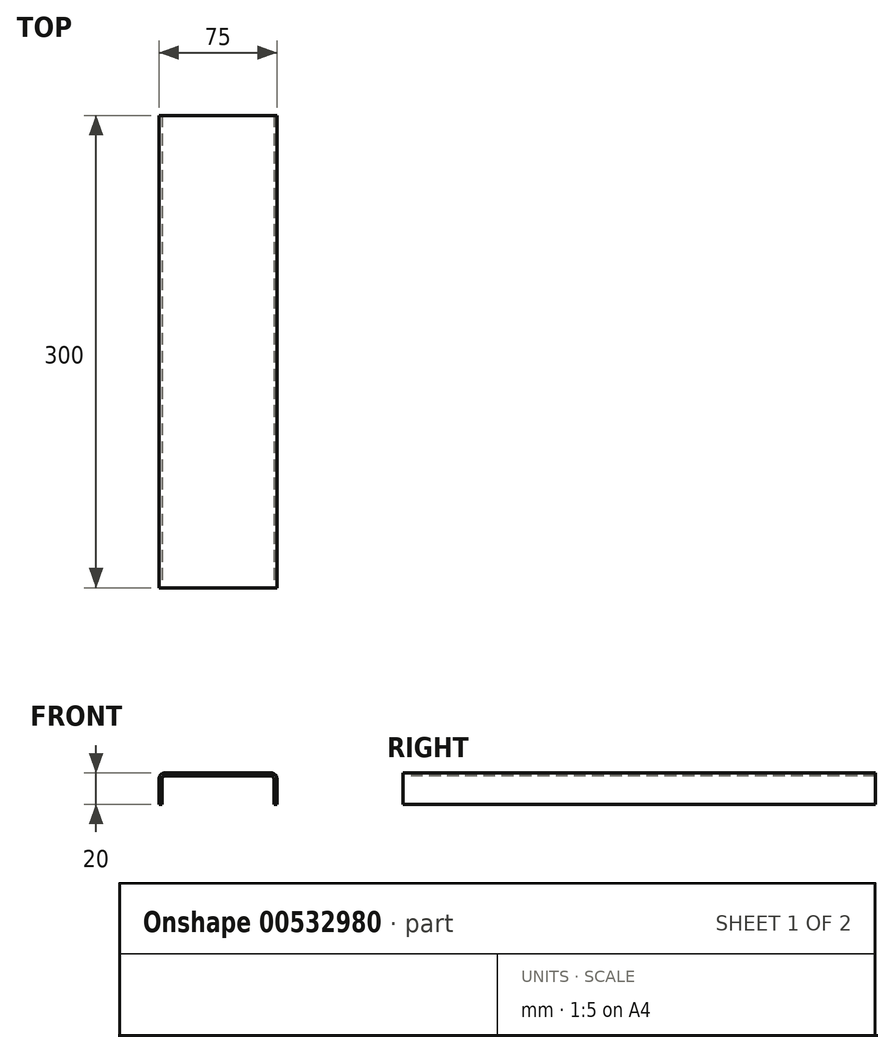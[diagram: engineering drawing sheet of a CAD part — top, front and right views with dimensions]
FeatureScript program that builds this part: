
annotation { "Feature Type Name" : "Feature", "Feature Type Description" : "" }
export const myFeature = defineFeature(function(context is Context, id is Id, definition is map)
    precondition{}
    {
        {
            var Q0;
            Q0=qCreatedBy(makeId("Front.planeOp"),FACE);
            var sketch = newSketch(context, id + "F0", { "sketchPlane" : qUnion([Q0])});
            skLineSegment(sketch, "E0", {"start": v(-85.73, 0) * mm, "end": v(-85.73, 16) * mm});
            skLineSegment(sketch, "E1", {"start": v(-81.73, 20) * mm, "end": v(-14.73, 20) * mm});
            skLineSegment(sketch, "E2", {"start": v(-10.73, 16) * mm, "end": v(-10.73, 0) * mm});
            skLineSegment(sketch, "E3.0", {"start": v(-12.73, 16) * mm, "end": v(-12.73, 0) * mm});
            skLineSegment(sketch, "E4.0", {"start": v(-81.73, 18) * mm, "end": v(-14.73, 18) * mm});
            skLineSegment(sketch, "E5.0", {"start": v(-83.73, 0) * mm, "end": v(-83.73, 16) * mm});
            skLineSegment(sketch, "E6", {"start": v(-83.73, 0) * mm, "end": v(-85.73, 0) * mm});
            skLineSegment(sketch, "E7", {"start": v(-10.73, 0) * mm, "end": v(-12.73, 0) * mm});
            skPoint(sketch, "E8.visualSharp", {"position": v(-12.73, 18) * mm});
            skArc(sketch, "E8.filletArc", {"start": v(-12.73, 16) * mm, "mid": v(-13.32, 17.41) * mm, "end": v(-14.73, 18) * mm});
            skPoint(sketch, "E9.visualSharp", {"position": v(-83.73, 18) * mm});
            skArc(sketch, "E9.filletArc", {"start": v(-81.73, 18) * mm, "mid": v(-83.15, 17.41) * mm, "end": v(-83.73, 16) * mm});
            skPoint(sketch, "E10.visualSharp", {"position": v(-85.73, 20) * mm});
            skArc(sketch, "E10.filletArc", {"start": v(-81.73, 20) * mm, "mid": v(-84.56, 18.83) * mm, "end": v(-85.73, 16) * mm});
            skPoint(sketch, "E11.visualSharp", {"position": v(-10.73, 20) * mm});
            skArc(sketch, "E11.filletArc", {"start": v(-10.73, 16) * mm, "mid": v(-11.9, 18.83) * mm, "end": v(-14.73, 20) * mm});
            skSolve(sketch);
        }
        {
            var Q0;
            Q0=makeQuery(id+"F0.imprint","IMPRINT",FACE,{"disambiguationData":[TD([[makeQuery(id+"F0.imprint","IMPRINT",EDGE,{"derivedFrom":sQuery(id+"F0.wireOp",EDGE,"E0")}),-1.0]])]});
            extrude(context, id + "F1", {"entities" : qUnion([Q0]), "oppositeDirection" : true, "depth" : 300 * mm, "offsetDistance" : 25 * mm});
        }
    });
